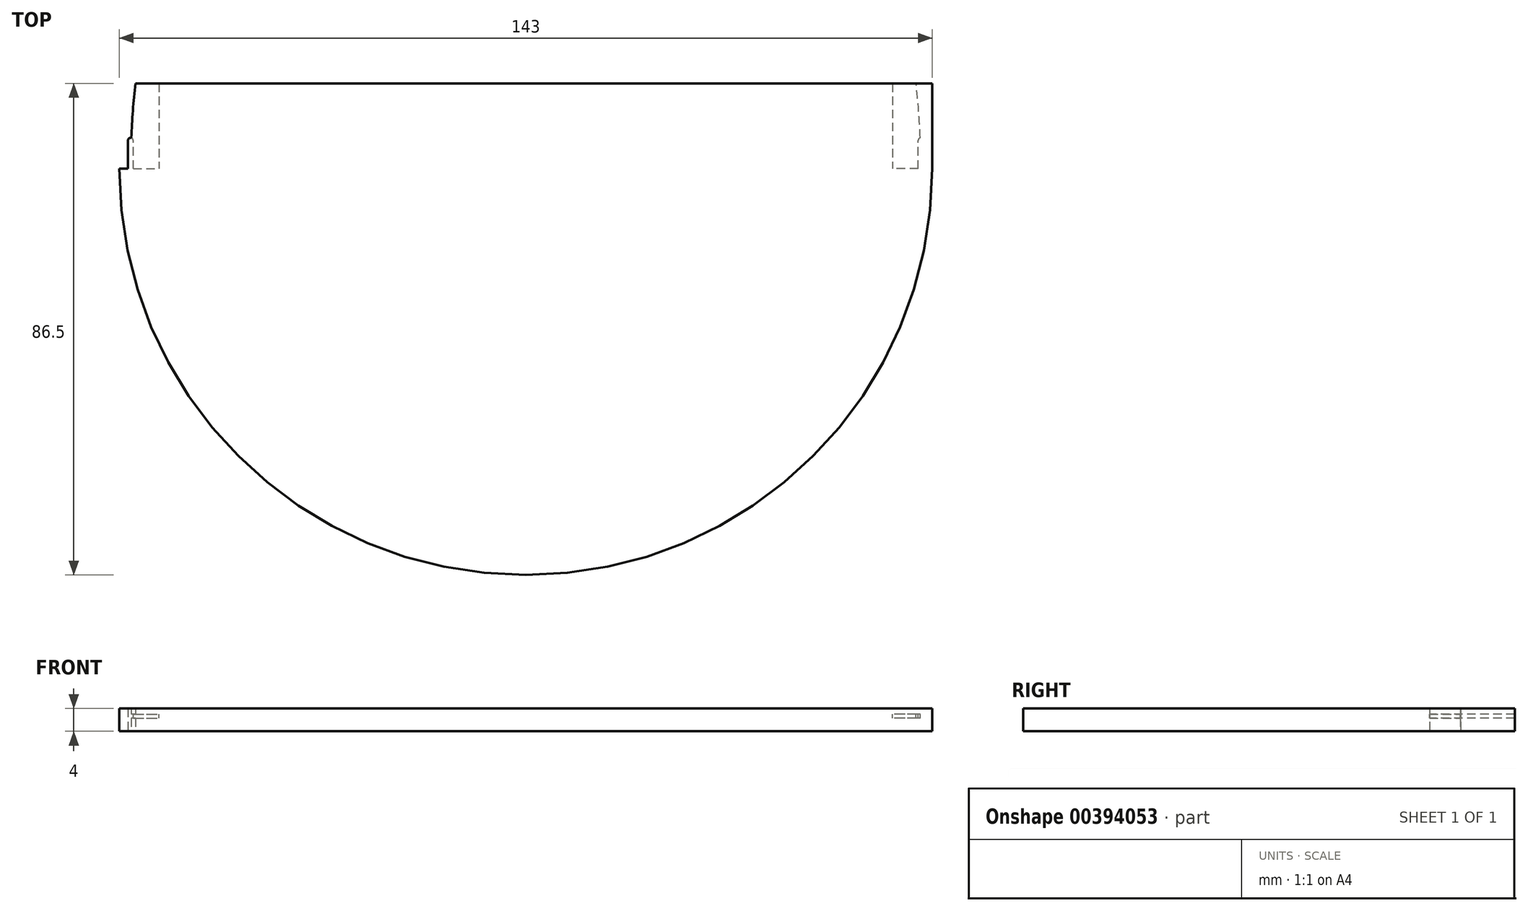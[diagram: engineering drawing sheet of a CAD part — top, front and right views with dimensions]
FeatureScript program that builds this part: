
annotation { "Feature Type Name" : "Feature", "Feature Type Description" : "" }
export const myFeature = defineFeature(function(context is Context, id is Id, definition is map)
    precondition{}
    {
        {
            var Q0;
            Q0=qCreatedBy(makeId("Top.planeOp"),FACE);
            var sketch = newSketch(context, id + "F0", { "sketchPlane" : qUnion([Q0])});
            skLineSegment(sketch, "E0", {"start": v(-64.5, 0) * mm, "end": v(-69.5, 0) * mm, "construction": true});
            skLineSegment(sketch, "E1", {"start": v(-69.5, 0) * mm, "end": v(-69.5, 5) * mm, "construction": true});
            skLineSegment(sketch, "E2.MirrorCS", {"start": v(69.5, 0) * mm, "end": v(69.5, 5) * mm, "construction": true});
            skLineSegment(sketch, "E3.MirrorCS", {"start": v(64.5, 0) * mm, "end": v(69.5, 0) * mm, "construction": true});
            skArc(sketch, "E4", {"start": v(-69.5, 0) * mm, "mid": v(-67.11, 25.18) * mm, "end": v(-60.04, 49.46) * mm});
            skArc(sketch, "E5.MirrorCS", {"start": v(69.5, 0) * mm, "mid": v(67.11, 25.18) * mm, "end": v(60.04, 49.46) * mm});
            skArc(sketch, "E6", {"start": v(-64.5, 0) * mm, "mid": v(-62.11, 24.7) * mm, "end": v(-55.05, 48.48) * mm, "construction": true});
            skArc(sketch, "E7.MirrorCS", {"start": v(64.5, 0) * mm, "mid": v(62.11, 24.7) * mm, "end": v(55.05, 48.48) * mm, "construction": true});
            skArc(sketch, "E8", {"start": v(69.5, 0) * mm, "mid": v(0, -69.5) * mm, "end": v(-69.5, 0) * mm, "construction": true});
            skArc(sketch, "E9.0", {"start": v(71.5, 0) * mm, "mid": v(0, -71.5) * mm, "end": v(-71.5, 0) * mm});
            skArc(sketch, "E10.0.endCap", {"start": v(-69.95, 5) * mm, "mid": v(-69.5, 5.45) * mm, "end": v(-69.05, 5) * mm});
            skLineSegment(sketch, "E10.0.left", {"start": v(-69.95, 0) * mm, "end": v(-69.95, 5) * mm});
            skLineSegment(sketch, "E10.0.right", {"start": v(-69.05, 0) * mm, "end": v(-69.05, 5) * mm});
            skLineSegment(sketch, "E11", {"start": v(-71.5, 0) * mm, "end": v(-71.5, 15) * mm});
            skLineSegment(sketch, "E12", {"start": v(-71.5, 15) * mm, "end": v(-64.5, 15) * mm});
            skLineSegment(sketch, "E13", {"start": v(-64.5, 15) * mm, "end": v(-64.5, 0) * mm});
            skLineSegment(sketch, "E14", {"start": v(-69.05, 0) * mm, "end": v(-64.5, 0) * mm});
            skLineSegment(sketch, "E15.MirrorCS", {"start": v(71.5, 0) * mm, "end": v(71.5, 15) * mm});
            skLineSegment(sketch, "E16.MirrorCS", {"start": v(71.5, 15) * mm, "end": v(64.5, 15) * mm});
            skLineSegment(sketch, "E17.MirrorCS", {"start": v(64.5, 15) * mm, "end": v(64.5, 0) * mm});
            skLineSegment(sketch, "E18.MirrorCS", {"start": v(69.05, 0) * mm, "end": v(64.5, 0) * mm});
            skLineSegment(sketch, "E19.MirrorCS", {"start": v(69.05, 0) * mm, "end": v(69.05, 5) * mm});
            skLineSegment(sketch, "E20.MirrorCS", {"start": v(69.95, 0) * mm, "end": v(69.95, 5) * mm});
            skArc(sketch, "E21.MirrorCS", {"start": v(69.95, 5) * mm, "mid": v(69.5, 5.45) * mm, "end": v(69.05, 5) * mm});
            skLineSegment(sketch, "E22", {"start": v(-71.5, 15) * mm, "end": v(71.5, 15) * mm});
            skLineSegment(sketch, "E23", {"start": v(-71.5, 0) * mm, "end": v(-69.95, 0) * mm});
            skLineSegment(sketch, "E24.MirrorCS", {"start": v(71.5, 0) * mm, "end": v(69.95, 0) * mm});
            skSolve(sketch);
        }
        {
            var Q0;
            Q0=makeQuery(id+"F0.imprint","IMPRINT",FACE,{"disambiguationData":[TD([[makeQuery(id+"F0.imprint","IMPRINT",EDGE,{"derivedFrom":sQuery(id+"F0.wireOp",EDGE,"E10.0.endCap")}),1.0]])]});
            var Q1;
            Q1=makeQuery(id+"F0.imprint","IMPRINT",FACE,{"disambiguationData":[TD([[makeQuery(id+"F0.imprint","IMPRINT",EDGE,{"derivedFrom":sQuery(id+"F0.wireOp",EDGE,"E9.0")}),-1.0]])]});
            var Q2;
            {var subQ1=sQuery(id+"F0.wireOp",EDGE,"E15.MirrorCS");Q2=makeQuery(id+"F0.imprint","IMPRINT",FACE,{"disambiguationData":[TD([[makeQuery(id+"F0.imprint","IMPRINT",EDGE,{"derivedFrom":subQ1}),1.0]])]});}
            var Q3;
            {var subQ1=sQuery(id+"F0.wireOp",EDGE,"E13");Q3=makeQuery(id+"F0.imprint","IMPRINT",FACE,{"disambiguationData":[TD([[makeQuery(id+"F0.imprint","IMPRINT",EDGE,{"derivedFrom":subQ1}),-1.0]])]});}
            var Q4;
            {var subQ6=sQuery(id+"F0.wireOp",EDGE,"E17.MirrorCS");Q4=makeQuery(id+"F0.imprint","IMPRINT",FACE,{"disambiguationData":[TD([[makeQuery(id+"F0.imprint","IMPRINT",EDGE,{"derivedFrom":subQ6}),1.0]])]});}
            extrude(context, id + "F1", {"entities" : qUnion([Q0, Q1, Q2, Q3, Q4]), "depth" : 1 * mm});
        }
        {
            var Q0;
            {var subQ1=sQuery(id+"F0.wireOp",EDGE,"E15.MirrorCS");Q0=makeQuery(id+"F0.imprint","IMPRINT",FACE,{"disambiguationData":[TD([[makeQuery(id+"F0.imprint","IMPRINT",EDGE,{"derivedFrom":subQ1}),1.0]])]});}
            var Q1;
            Q1=makeQuery(id+"F0.imprint","IMPRINT",FACE,{"disambiguationData":[TD([[makeQuery(id+"F0.imprint","IMPRINT",EDGE,{"derivedFrom":sQuery(id+"F0.wireOp",EDGE,"E10.0.endCap")}),1.0]])]});
            var Q2;
            {var subQ1=sQuery(id+"F0.wireOp",EDGE,"E13");Q2=makeQuery(id+"F0.imprint","IMPRINT",FACE,{"disambiguationData":[TD([[makeQuery(id+"F0.imprint","IMPRINT",EDGE,{"derivedFrom":subQ1}),-1.0]])]});}
            var Q3;
            {var subQ6=sQuery(id+"F0.wireOp",EDGE,"E17.MirrorCS");Q3=makeQuery(id+"F0.imprint","IMPRINT",FACE,{"disambiguationData":[TD([[makeQuery(id+"F0.imprint","IMPRINT",EDGE,{"derivedFrom":subQ6}),1.0]])]});}
            extrude(context, id + "F2", {"entities" : qUnion([Q0, Q1, Q2, Q3]), "operationType" : NewBodyOperationType.ADD, "oppositeDirection" : true, "depth" : 3 * mm});
        }
        {
            var Q0;
            {var subQ1=sQuery(id+"F0.wireOp",EDGE,"E13");Q0=makeQuery(id+"F0.imprint","IMPRINT",FACE,{"disambiguationData":[TD([[makeQuery(id+"F0.imprint","IMPRINT",EDGE,{"derivedFrom":subQ1}),-1.0]])]});}
            var Q1;
            {var subQ6=sQuery(id+"F0.wireOp",EDGE,"E17.MirrorCS");Q1=makeQuery(id+"F0.imprint","IMPRINT",FACE,{"disambiguationData":[TD([[makeQuery(id+"F0.imprint","IMPRINT",EDGE,{"derivedFrom":subQ6}),1.0]])]});}
            extrude(context, id + "F3", {"entities" : qUnion([Q0, Q1]), "operationType" : NewBodyOperationType.REMOVE, "oppositeDirection" : true, "depth" : 0.7 * mm});
        }
    });
